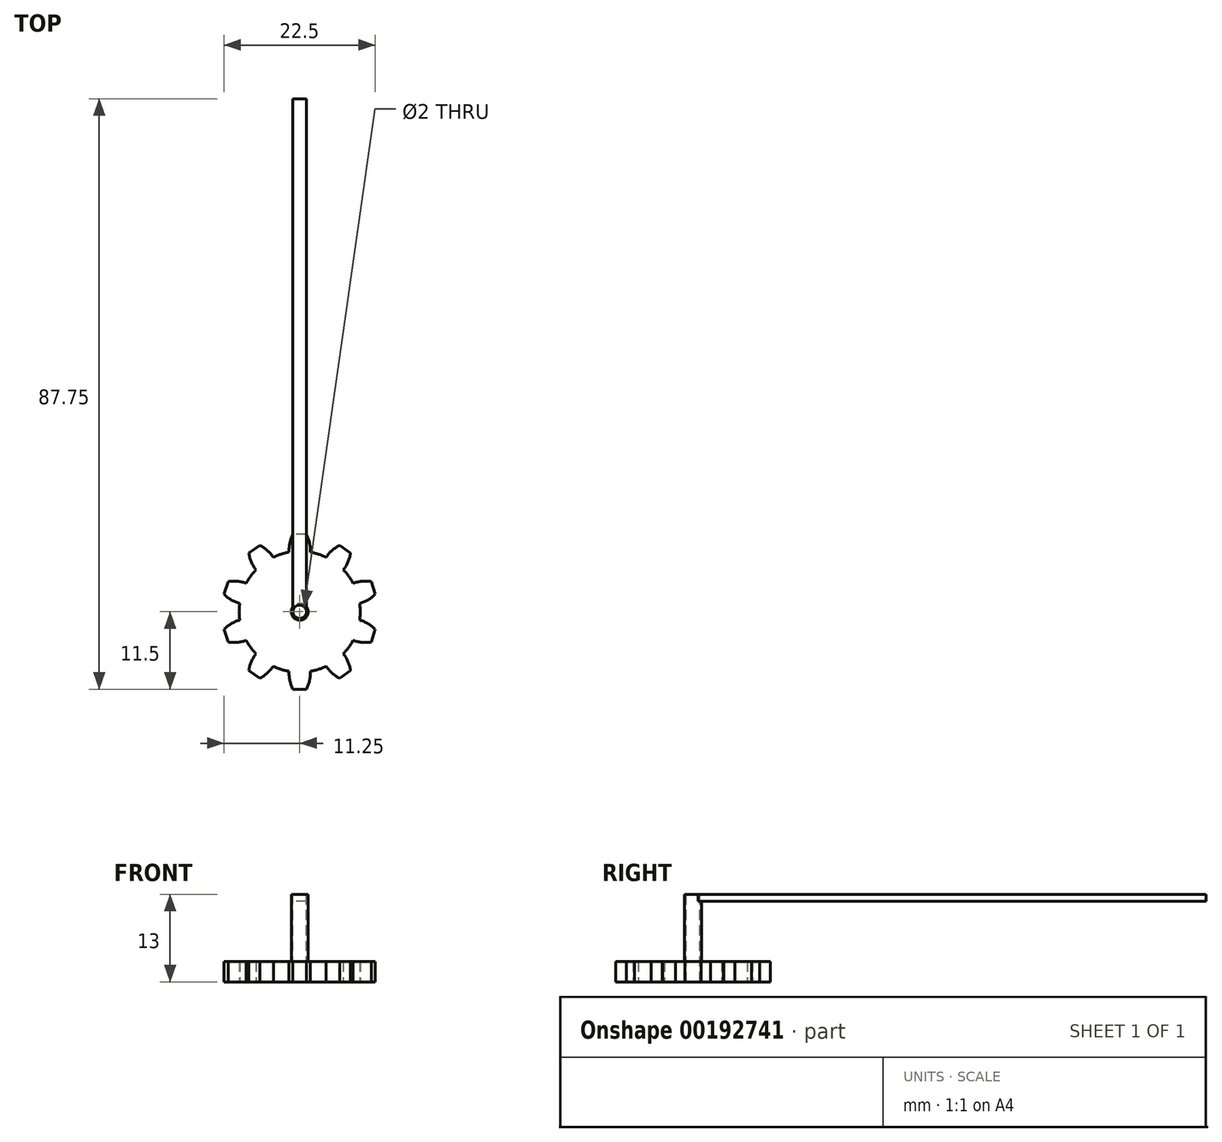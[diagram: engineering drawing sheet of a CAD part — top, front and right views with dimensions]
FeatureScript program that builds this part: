
annotation { "Feature Type Name" : "Feature", "Feature Type Description" : "" }
export const myFeature = defineFeature(function(context is Context, id is Id, definition is map)
    precondition{}
    {
        {
            var Q0;
            Q0=qCreatedBy(makeId("Top.planeOp"),FACE);
            var sketch = newSketch(context, id + "F0", { "sketchPlane" : qUnion([Q0])});
            skCircle(sketch, "E0", {"center": v(0, 0) * mm, "radius": 9 * mm});
            skLineSegment(sketch, "E1", {"start": v(0, 0) * mm, "end": v(0, 9) * mm, "construction": true});
            skLineSegment(sketch, "E2", {"start": v(0, 11.5) * mm, "end": v(-1, 11.5) * mm});
            skArc(sketch, "E3", {"start": v(-1, 11.5) * mm, "mid": v(-1.46, 10.22) * mm, "end": v(-1.59, 8.86) * mm});
            skLineSegment(sketch, "E4.MirrorCS", {"start": v(0, 11.5) * mm, "end": v(1, 11.5) * mm});
            skArc(sketch, "E5.MirrorCS", {"start": v(1, 11.5) * mm, "mid": v(1.46, 10.22) * mm, "end": v(1.59, 8.86) * mm});
            skArc(sketch, "E6.1.0", {"start": v(-7.57, 8.72) * mm, "mid": v(-7.18, 7.4) * mm, "end": v(-6.5, 6.23) * mm});
            skLineSegment(sketch, "E6.1.1", {"start": v(-6.76, 9.3) * mm, "end": v(-7.57, 8.72) * mm});
            skLineSegment(sketch, "E6.1.2", {"start": v(-6.76, 9.3) * mm, "end": v(-5.95, 9.9) * mm});
            skArc(sketch, "E6.1.3", {"start": v(-5.95, 9.9) * mm, "mid": v(-4.83, 9.12) * mm, "end": v(-3.92, 8.1) * mm});
            skArc(sketch, "E6.2.0", {"start": v(-11.25, 2.6) * mm, "mid": v(-10.17, 1.77) * mm, "end": v(-8.92, 1.23) * mm});
            skLineSegment(sketch, "E6.2.1", {"start": v(-10.94, 3.55) * mm, "end": v(-11.25, 2.6) * mm});
            skLineSegment(sketch, "E6.2.2", {"start": v(-10.94, 3.55) * mm, "end": v(-10.63, 4.5) * mm});
            skArc(sketch, "E6.2.3", {"start": v(-10.63, 4.5) * mm, "mid": v(-9.27, 4.54) * mm, "end": v(-7.93, 4.25) * mm});
            skArc(sketch, "E6.3.0", {"start": v(-10.63, -4.5) * mm, "mid": v(-9.27, -4.54) * mm, "end": v(-7.93, -4.25) * mm});
            skLineSegment(sketch, "E6.3.1", {"start": v(-10.94, -3.55) * mm, "end": v(-10.63, -4.5) * mm});
            skLineSegment(sketch, "E6.3.2", {"start": v(-10.94, -3.55) * mm, "end": v(-11.25, -2.6) * mm});
            skArc(sketch, "E6.3.3", {"start": v(-11.25, -2.6) * mm, "mid": v(-10.17, -1.77) * mm, "end": v(-8.92, -1.23) * mm});
            skArc(sketch, "E6.4.0", {"start": v(-5.95, -9.9) * mm, "mid": v(-4.83, -9.12) * mm, "end": v(-3.92, -8.1) * mm});
            skLineSegment(sketch, "E6.4.1", {"start": v(-6.76, -9.3) * mm, "end": v(-5.95, -9.9) * mm});
            skLineSegment(sketch, "E6.4.2", {"start": v(-6.76, -9.3) * mm, "end": v(-7.57, -8.72) * mm});
            skArc(sketch, "E6.4.3", {"start": v(-7.57, -8.72) * mm, "mid": v(-7.18, -7.4) * mm, "end": v(-6.5, -6.23) * mm});
            skArc(sketch, "E6.5.0", {"start": v(1, -11.5) * mm, "mid": v(1.46, -10.22) * mm, "end": v(1.59, -8.86) * mm});
            skLineSegment(sketch, "E6.5.1", {"start": v(0, -11.5) * mm, "end": v(1, -11.5) * mm});
            skLineSegment(sketch, "E6.5.2", {"start": v(0, -11.5) * mm, "end": v(-1, -11.5) * mm});
            skArc(sketch, "E6.5.3", {"start": v(-1, -11.5) * mm, "mid": v(-1.46, -10.22) * mm, "end": v(-1.59, -8.86) * mm});
            skArc(sketch, "E7.3.6.0", {"start": v(7.57, -8.72) * mm, "mid": v(7.18, -7.4) * mm, "end": v(6.5, -6.23) * mm});
            skLineSegment(sketch, "E7.4.6.0", {"start": v(6.76, -9.3) * mm, "end": v(7.57, -8.72) * mm});
            skLineSegment(sketch, "E7.7.6.0", {"start": v(6.76, -9.3) * mm, "end": v(5.95, -9.9) * mm});
            skArc(sketch, "E7.10.6.0", {"start": v(5.95, -9.9) * mm, "mid": v(4.83, -9.12) * mm, "end": v(3.92, -8.1) * mm});
            skArc(sketch, "E7.3.7.0", {"start": v(11.25, -2.6) * mm, "mid": v(10.17, -1.77) * mm, "end": v(8.92, -1.23) * mm});
            skLineSegment(sketch, "E7.4.7.0", {"start": v(10.94, -3.55) * mm, "end": v(11.25, -2.6) * mm});
            skLineSegment(sketch, "E7.7.7.0", {"start": v(10.94, -3.55) * mm, "end": v(10.63, -4.5) * mm});
            skArc(sketch, "E7.10.7.0", {"start": v(10.63, -4.5) * mm, "mid": v(9.27, -4.54) * mm, "end": v(7.93, -4.25) * mm});
            skArc(sketch, "E7.3.8.0", {"start": v(10.63, 4.5) * mm, "mid": v(9.27, 4.54) * mm, "end": v(7.93, 4.25) * mm});
            skLineSegment(sketch, "E7.4.8.0", {"start": v(10.94, 3.55) * mm, "end": v(10.63, 4.5) * mm});
            skLineSegment(sketch, "E7.7.8.0", {"start": v(10.94, 3.55) * mm, "end": v(11.25, 2.6) * mm});
            skArc(sketch, "E7.10.8.0", {"start": v(11.25, 2.6) * mm, "mid": v(10.17, 1.77) * mm, "end": v(8.92, 1.23) * mm});
            skArc(sketch, "E7.3.9.0", {"start": v(5.95, 9.9) * mm, "mid": v(4.83, 9.12) * mm, "end": v(3.92, 8.1) * mm});
            skLineSegment(sketch, "E7.4.9.0", {"start": v(6.76, 9.3) * mm, "end": v(5.95, 9.9) * mm});
            skLineSegment(sketch, "E7.7.9.0", {"start": v(6.76, 9.3) * mm, "end": v(7.57, 8.72) * mm});
            skArc(sketch, "E7.10.9.0", {"start": v(7.57, 8.72) * mm, "mid": v(7.18, 7.4) * mm, "end": v(6.5, 6.23) * mm});
            skSolve(sketch);
        }
        {
            var Q0;
            Q0 = qSketchRegion(id + "F0", true);
            extrude(context, id + "F1", {"entities" : qUnion([Q0]), "depth" : 3 * mm});
        }
        {
            var Q0;
            Q0=makeQuery(id+"F1.opExtrude","CAP_FACE",FACE,{"disambiguationData":[OSD([sQuery(id+"F0.wireOp",EDGE,"E0"),sQuery(id+"F0.wireOp",EDGE,"E2"),sQuery(id+"F0.wireOp",EDGE,"E3"),sQuery(id+"F0.wireOp",EDGE,"E4.MirrorCS"),sQuery(id+"F0.wireOp",EDGE,"E5.MirrorCS"),sQuery(id+"F0.wireOp",EDGE,"E6.1.0"),sQuery(id+"F0.wireOp",EDGE,"E6.1.1"),sQuery(id+"F0.wireOp",EDGE,"E6.1.2"),sQuery(id+"F0.wireOp",EDGE,"E6.1.3"),sQuery(id+"F0.wireOp",EDGE,"E6.2.0"),sQuery(id+"F0.wireOp",EDGE,"E6.2.1"),sQuery(id+"F0.wireOp",EDGE,"E6.2.2"),sQuery(id+"F0.wireOp",EDGE,"E6.2.3"),sQuery(id+"F0.wireOp",EDGE,"E6.3.0"),sQuery(id+"F0.wireOp",EDGE,"E6.3.1"),sQuery(id+"F0.wireOp",EDGE,"E6.3.2"),sQuery(id+"F0.wireOp",EDGE,"E6.3.3"),sQuery(id+"F0.wireOp",EDGE,"E6.4.0"),sQuery(id+"F0.wireOp",EDGE,"E6.4.1"),sQuery(id+"F0.wireOp",EDGE,"E6.4.2"),sQuery(id+"F0.wireOp",EDGE,"E6.4.3"),sQuery(id+"F0.wireOp",EDGE,"E6.5.0"),sQuery(id+"F0.wireOp",EDGE,"E6.5.1"),sQuery(id+"F0.wireOp",EDGE,"E6.5.2"),sQuery(id+"F0.wireOp",EDGE,"E6.5.3"),sQuery(id+"F0.wireOp",EDGE,"E6.6.0"),sQuery(id+"F0.wireOp",EDGE,"E6.6.1"),sQuery(id+"F0.wireOp",EDGE,"E6.6.2"),sQuery(id+"F0.wireOp",EDGE,"E6.6.3"),sQuery(id+"F0.wireOp",EDGE,"E6.7.0"),sQuery(id+"F0.wireOp",EDGE,"E6.7.1"),sQuery(id+"F0.wireOp",EDGE,"E6.7.2"),sQuery(id+"F0.wireOp",EDGE,"E6.7.3"),sQuery(id+"F0.wireOp",EDGE,"E6.8.0"),sQuery(id+"F0.wireOp",EDGE,"E6.8.1"),sQuery(id+"F0.wireOp",EDGE,"E6.8.2"),sQuery(id+"F0.wireOp",EDGE,"E6.8.3"),sQuery(id+"F0.wireOp",EDGE,"E6.9.0"),sQuery(id+"F0.wireOp",EDGE,"E6.9.1"),sQuery(id+"F0.wireOp",EDGE,"E6.9.2"),sQuery(id+"F0.wireOp",EDGE,"E6.9.3"),sQuery(id+"F0.wireOp",EDGE,"E6.10.0"),sQuery(id+"F0.wireOp",EDGE,"E6.10.1"),sQuery(id+"F0.wireOp",EDGE,"E6.10.2"),sQuery(id+"F0.wireOp",EDGE,"E6.10.3"),sQuery(id+"F0.wireOp",EDGE,"E6.11.0"),sQuery(id+"F0.wireOp",EDGE,"E6.11.1"),sQuery(id+"F0.wireOp",EDGE,"E6.11.2"),sQuery(id+"F0.wireOp",EDGE,"E6.11.3"),sQuery(id+"F0.wireOp",EDGE,"E6.12.0"),sQuery(id+"F0.wireOp",EDGE,"E6.12.1"),sQuery(id+"F0.wireOp",EDGE,"E6.12.2"),sQuery(id+"F0.wireOp",EDGE,"E6.12.3"),sQuery(id+"F0.wireOp",EDGE,"E6.13.0"),sQuery(id+"F0.wireOp",EDGE,"E6.13.1"),sQuery(id+"F0.wireOp",EDGE,"E6.13.2"),sQuery(id+"F0.wireOp",EDGE,"E6.13.3"),sQuery(id+"F0.wireOp",EDGE,"E6.14.0"),sQuery(id+"F0.wireOp",EDGE,"E6.14.1"),sQuery(id+"F0.wireOp",EDGE,"E6.14.2"),sQuery(id+"F0.wireOp",EDGE,"E6.14.3"),sQuery(id+"F0.wireOp",EDGE,"E6.15.0"),sQuery(id+"F0.wireOp",EDGE,"E6.15.1"),sQuery(id+"F0.wireOp",EDGE,"E6.15.2"),sQuery(id+"F0.wireOp",EDGE,"E6.15.3")])],"isStart":false});
            var sketch = newSketch(context, id + "F2", { "sketchPlane" : qUnion([Q0])});
            skCircle(sketch, "E8", {"center": v(0, 0) * mm, "radius": 1.25 * mm});
            skSolve(sketch);
        }
        {
            var Q0;
            Q0 = qSketchRegion(id + "F2", true);
            extrude(context, id + "F3", {"entities" : qUnion([Q0]), "operationType" : NewBodyOperationType.ADD, "depth" : 10 * mm});
        }
        {
            var Q0;
            Q0=makeQuery(id+"F3.opExtrude","CAP_FACE",FACE,{"disambiguationData":[OSD([sQuery(id+"F2.wireOp",EDGE,"E8")])],"isStart":false});
            var sketch = newSketch(context, id + "F4", { "sketchPlane" : qUnion([Q0])});
            skCircle(sketch, "E9", {"center": v(0, 0) * mm, "radius": 1 * mm});
            skSolve(sketch);
        }
        {
            var Q0;
            Q0 = qSketchRegion(id + "F4", true);
            extrude(context, id + "F5", {"entities" : qUnion([Q0]), "operationType" : NewBodyOperationType.REMOVE, "oppositeDirection" : true, "depth" : 25 * mm});
        }
        {
            var Q0;
            Q0=makeQuery(id+"F3.opExtrude","CAP_FACE",FACE,{"disambiguationData":[OSD([sQuery(id+"F2.wireOp",EDGE,"E8")])],"isStart":false});
            var sketch = newSketch(context, id + "F6", { "sketchPlane" : qUnion([Q0])});
            skLineSegment(sketch, "E10.bottom", {"start": v(0, 1.25) * mm, "end": v(-1, 1.25) * mm});
            skLineSegment(sketch, "E10.top", {"start": v(0, 76.25) * mm, "end": v(-1, 76.25) * mm});
            skLineSegment(sketch, "E10.left", {"start": v(0, 1.25) * mm, "end": v(0, 76.25) * mm});
            skLineSegment(sketch, "E10.right", {"start": v(-1, 1.25) * mm, "end": v(-1, 76.25) * mm});
            skLineSegment(sketch, "E11.MirrorCS", {"start": v(1, 1.25) * mm, "end": v(1, 76.25) * mm});
            skLineSegment(sketch, "E12.MirrorCS", {"start": v(0, 76.25) * mm, "end": v(1, 76.25) * mm});
            skLineSegment(sketch, "E13.MirrorCS", {"start": v(0, 1.25) * mm, "end": v(1, 1.25) * mm});
            skLineSegment(sketch, "E14", {"start": v(-1, 1.25) * mm, "end": v(-1, 0.75) * mm});
            skLineSegment(sketch, "E15", {"start": v(1, 1.25) * mm, "end": v(1, 0.75) * mm});
            skArc(sketch, "E16", {"start": v(-1, 0.75) * mm, "mid": v(0, 1.25) * mm, "end": v(1, 0.75) * mm});
            skSolve(sketch);
        }
        {
            var Q0;
            Q0 = qSketchRegion(id + "F6", true);
            extrude(context, id + "F7", {"entities" : qUnion([Q0]), "operationType" : NewBodyOperationType.ADD, "oppositeDirection" : true, "depth" : 1 * mm});
        }
    });
